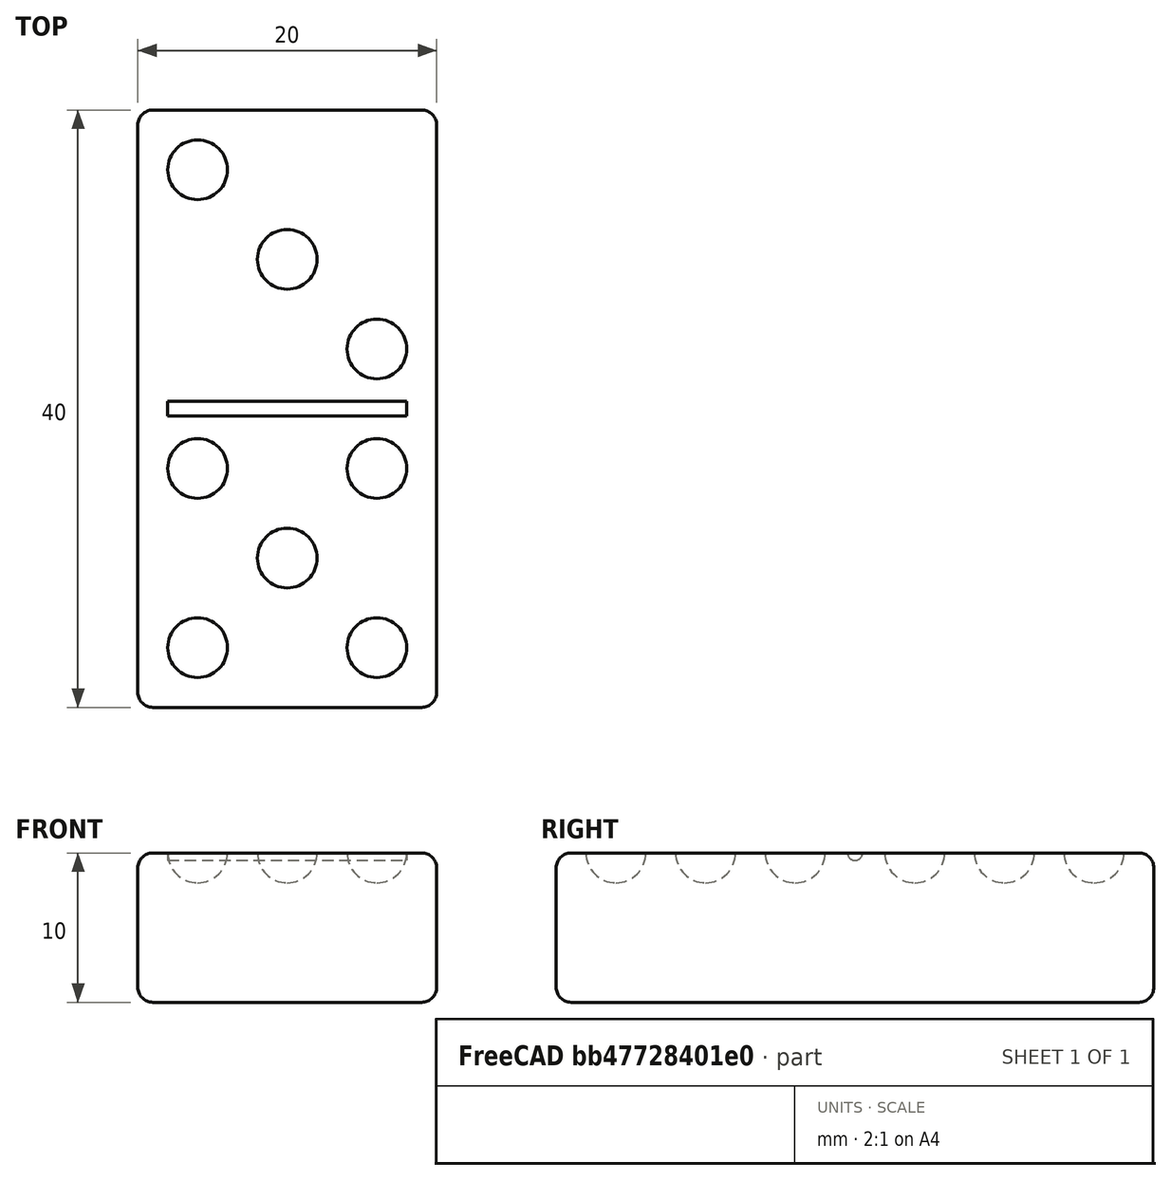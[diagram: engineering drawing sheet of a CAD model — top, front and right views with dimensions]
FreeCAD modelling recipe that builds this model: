
FCSTD DOCUMENT  (FreeCAD 0.18.4R)
Label: tutorial_freecad_ex13_d
License: All rights reserved
LicenseURL: http://en.wikipedia.org/wiki/All_rights_reserved
objects: Part::Sphere×3, Part::FeaturePython×3, Part::MultiFuse×3, Part::Box×1, Part::Fillet×1, Part::Cylinder×1, Part::Cut×1
note: 13 computed .brp shape members not serialized (recipe doc carries the construction recipe); baked Part::Feature solids carry a one-line shape summary decoded from their .brp

FEATURE [Part::Box] Box  label="Cubo"
  AttacherType = Attacher::AttachEngine3D
  Height = 10
  Length = 20
  Width = 40
FEATURE [Part::Fillet] Fillet  label="pastilla"
  Base = -> Box
  Edges = 12 edges r=1: [Edge1,Edge2,Edge3,Edge4,Edge5,Edge6,Edge7,Edge8,Edge9,Edge10,Edge11,Edge12]
FEATURE [Part::Cylinder] Cylinder  label="division"
  Angle = 360
  AttacherType = Attacher::AttachEngine3D
  Height = 16
  Placement = pos=(2,20,10) rot=(0,1,0;1.5708rad)
  Radius = 0.5
FEATURE [Part::Sphere] Sphere  label="Esfera"
  Angle1 = -90
  Angle2 = 90
  Angle3 = 360
  AttacherType = Attacher::AttachEngine3D
  Radius = 2
FEATURE [Part::FeaturePython] Array  label="tres"  # Draft array (typed FeaturePython)
  Angle = 360
  ArrayType = 0
  Axis = (0,0,1)
  Base = -> Sphere
  Center = (0,0,0)
  Fuse = false
  IntervalAxis = (0,0,0)
  IntervalX = (6,6,0)
  IntervalY = (0,1,0)
  IntervalZ = (0,0,1)
  NumberPolar = 1
  NumberX = 3
  NumberY = 1
  NumberZ = 1
  Placement = pos=(16,24,10) rot=(0,0,1;1.5708rad)
FEATURE [Part::Sphere] Sphere001  label="Esfera001"
  Angle1 = -90
  Angle2 = 90
  Angle3 = 360
  AttacherType = Attacher::AttachEngine3D
  Radius = 2
FEATURE [Part::FeaturePython] Array001  # Draft array (typed FeaturePython)
  Angle = 360
  ArrayType = 0
  Axis = (0,0,1)
  Base = -> Sphere001
  Center = (0,0,0)
  Fuse = false
  IntervalAxis = (0,0,0)
  IntervalX = (6,6,0)
  IntervalY = (0,1,0)
  IntervalZ = (0,0,1)
  NumberPolar = 1
  NumberX = 3
  NumberY = 1
  NumberZ = 1
  Placement = pos=(12,0,0) rot=(0,0,1;1.5708rad)
FEATURE [Part::Sphere] Sphere002  label="Esfera002"
  Angle1 = -90
  Angle2 = 90
  Angle3 = 360
  AttacherType = Attacher::AttachEngine3D
  Radius = 2
FEATURE [Part::FeaturePython] Array002  # Draft array (typed FeaturePython)
  Angle = 360
  ArrayType = 0
  Axis = (0,0,1)
  Base = -> Sphere002
  Center = (0,0,0)
  Fuse = false
  IntervalAxis = (0,0,0)
  IntervalX = (6,6,0)
  IntervalY = (0,1,0)
  IntervalZ = (0,0,1)
  NumberPolar = 1
  NumberX = 3
  NumberY = 1
  NumberZ = 1
FEATURE [Part::MultiFuse] Fusion  label="cinco"
  Placement = pos=(4,4,10) rot=(0,0,1;0rad)
  Refine = true
  Shapes = -> [Array001,Array002]
FEATURE [Part::MultiFuse] Fusion001  label="numeros_tres_cinco"
  Refine = true
  Shapes = -> [Array,Fusion]
FEATURE [Part::MultiFuse] Fusion002  label="grabado_tres_cinco"
  Refine = true
  Shapes = -> [Fusion001,Cylinder]
FEATURE [Part::Cut] Cut  label="pieza_tres_cicno"
  Base = -> Fillet
  Refine = true
  Tool = -> Fusion002
